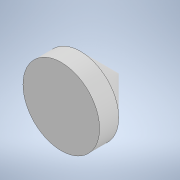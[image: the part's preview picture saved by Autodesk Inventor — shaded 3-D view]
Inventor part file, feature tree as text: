
AUTODESK INVENTOR PART (.ipt)
format: ipt  version: 2020 (Build 240168000, 168)  size: 102,400 bytes
history: native  units: in
note: dims shown in document units (in); Inventor stores cm internally (conversion verified against a paired STEP export)
features: revolve x1, sketch x1
ambient origin geometry x8: Origin, YZ Plane, XZ Plane, XY Plane, X Axis, Y Axis, Z Axis, Center Point
bodies: Body1 (feature_tree)
feature tree (2):
  revolve  "Revolution2"  [1 undecoded]
  sketch  "Sketch4"  dims[d7=0.7874in d8=1.1811in d10=90.0deg d12=0.7874in]
note: 1 required parameter value undecoded (feature->parameter linkage not recoverable at this tier; creation-order binding heuristic only, values carry confidence <= 0.55)
